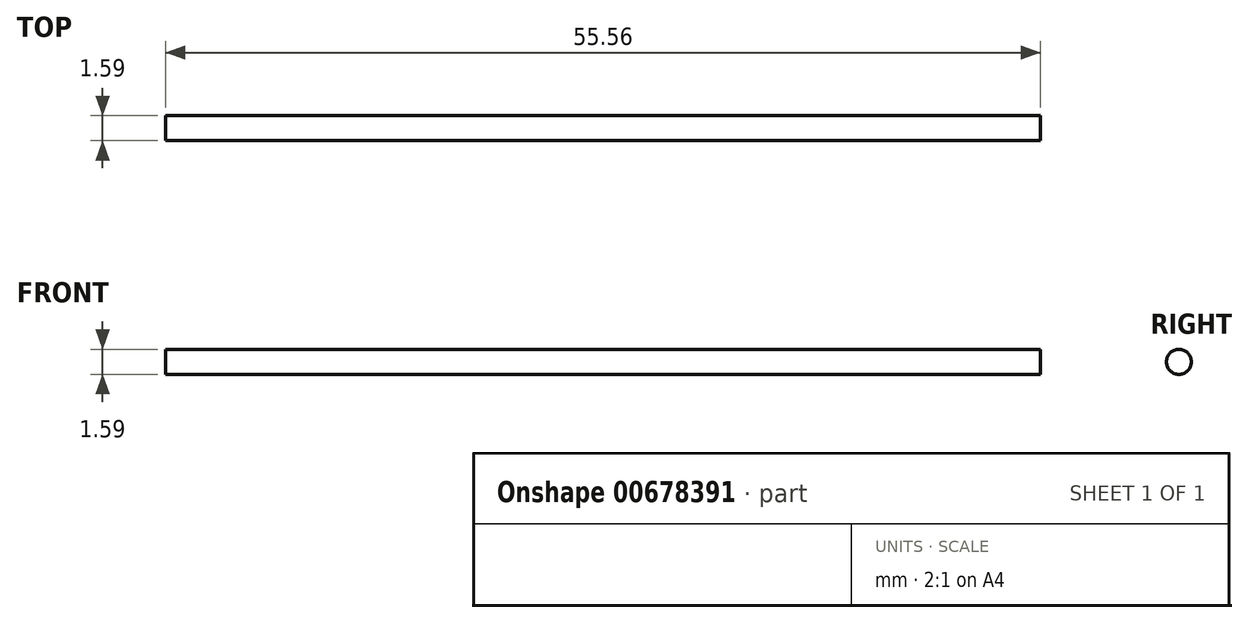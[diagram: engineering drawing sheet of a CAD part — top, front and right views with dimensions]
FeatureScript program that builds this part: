
annotation { "Feature Type Name" : "Feature", "Feature Type Description" : "" }
export const myFeature = defineFeature(function(context is Context, id is Id, definition is map)
    precondition{}
    {
        {
            var Q0;
            Q0=qCreatedBy(makeId("Right.planeOp"),FACE);
            var sketch = newSketch(context, id + "F0", { "sketchPlane" : qUnion([Q0])});
            skCircle(sketch, "E0", {"center": v(-40.9, 25.27) * mm, "radius": 0.8 * mm});
            skSolve(sketch);
        }
        {
            var Q0;
            Q0=makeQuery(id+"F0.imprint","IMPRINT",FACE,{"disambiguationData":[TD([[makeQuery(id+"F0.imprint","IMPRINT",EDGE,{"derivedFrom":sQuery(id+"F0.wireOp",EDGE,"E0")}),1.0]])]});
            extrude(context, id + "F1", {"entities" : qUnion([Q0]), "oppositeDirection" : true, "depth" : 55.56 * mm, "offsetDistance" : 25.4 * mm});
        }
    });
